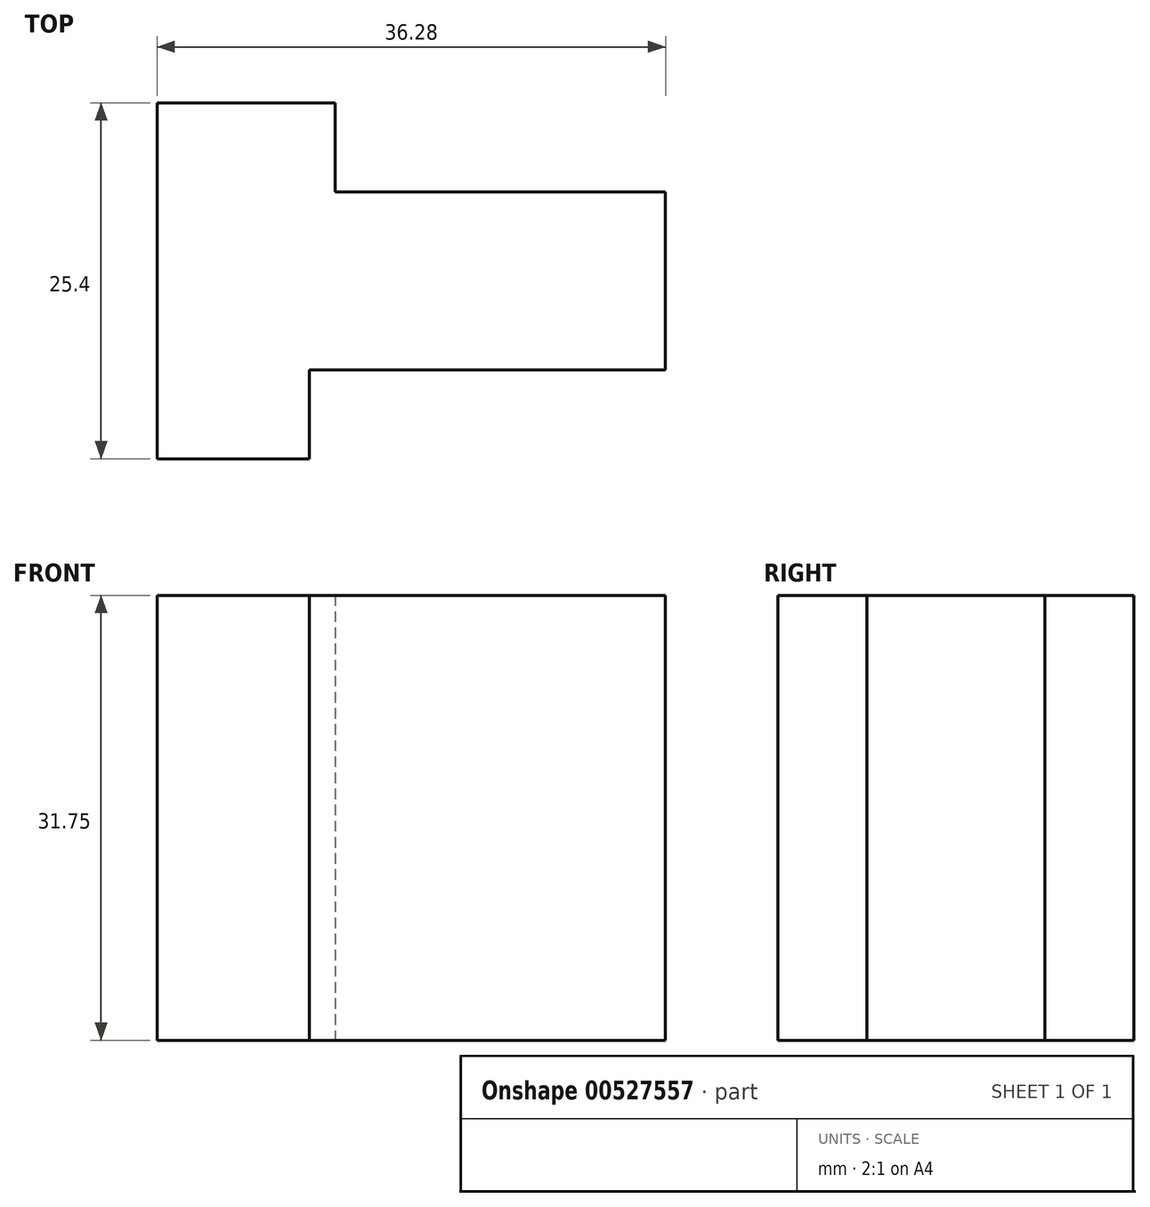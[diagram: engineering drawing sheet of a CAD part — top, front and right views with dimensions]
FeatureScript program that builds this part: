
annotation { "Feature Type Name" : "Feature", "Feature Type Description" : "" }
export const myFeature = defineFeature(function(context is Context, id is Id, definition is map)
    precondition{}
    {
        {
            var Q0;
            Q0=qCreatedBy(makeId("Top.planeOp"),FACE);
            var sketch = newSketch(context, id + "F0", { "sketchPlane" : qUnion([Q0])});
            skLineSegment(sketch, "E0", {"start": v(0, 0) * mm, "end": v(0, 25.4) * mm});
            skLineSegment(sketch, "E1", {"start": v(0, 25.4) * mm, "end": v(12.7, 25.4) * mm});
            skLineSegment(sketch, "E2", {"start": v(12.7, 25.4) * mm, "end": v(12.7, 19.05) * mm});
            skLineSegment(sketch, "E3", {"start": v(12.7, 19.05) * mm, "end": v(36.28, 19.05) * mm});
            skLineSegment(sketch, "E4", {"start": v(36.28, 19.05) * mm, "end": v(36.28, 6.35) * mm});
            skLineSegment(sketch, "E5", {"start": v(36.28, 6.35) * mm, "end": v(10.88, 6.35) * mm});
            skLineSegment(sketch, "E6", {"start": v(10.88, 6.35) * mm, "end": v(10.88, 0) * mm});
            skLineSegment(sketch, "E7", {"start": v(10.88, 0) * mm, "end": v(0, 0) * mm});
            skSolve(sketch);
        }
        {
            var Q0;
            Q0 = qSketchRegion(id + "F0", true);
            extrude(context, id + "F1", {"entities" : qUnion([Q0]), "depth" : 31.75 * mm, "offsetDistance" : 25.4 * mm});
        }
    });
